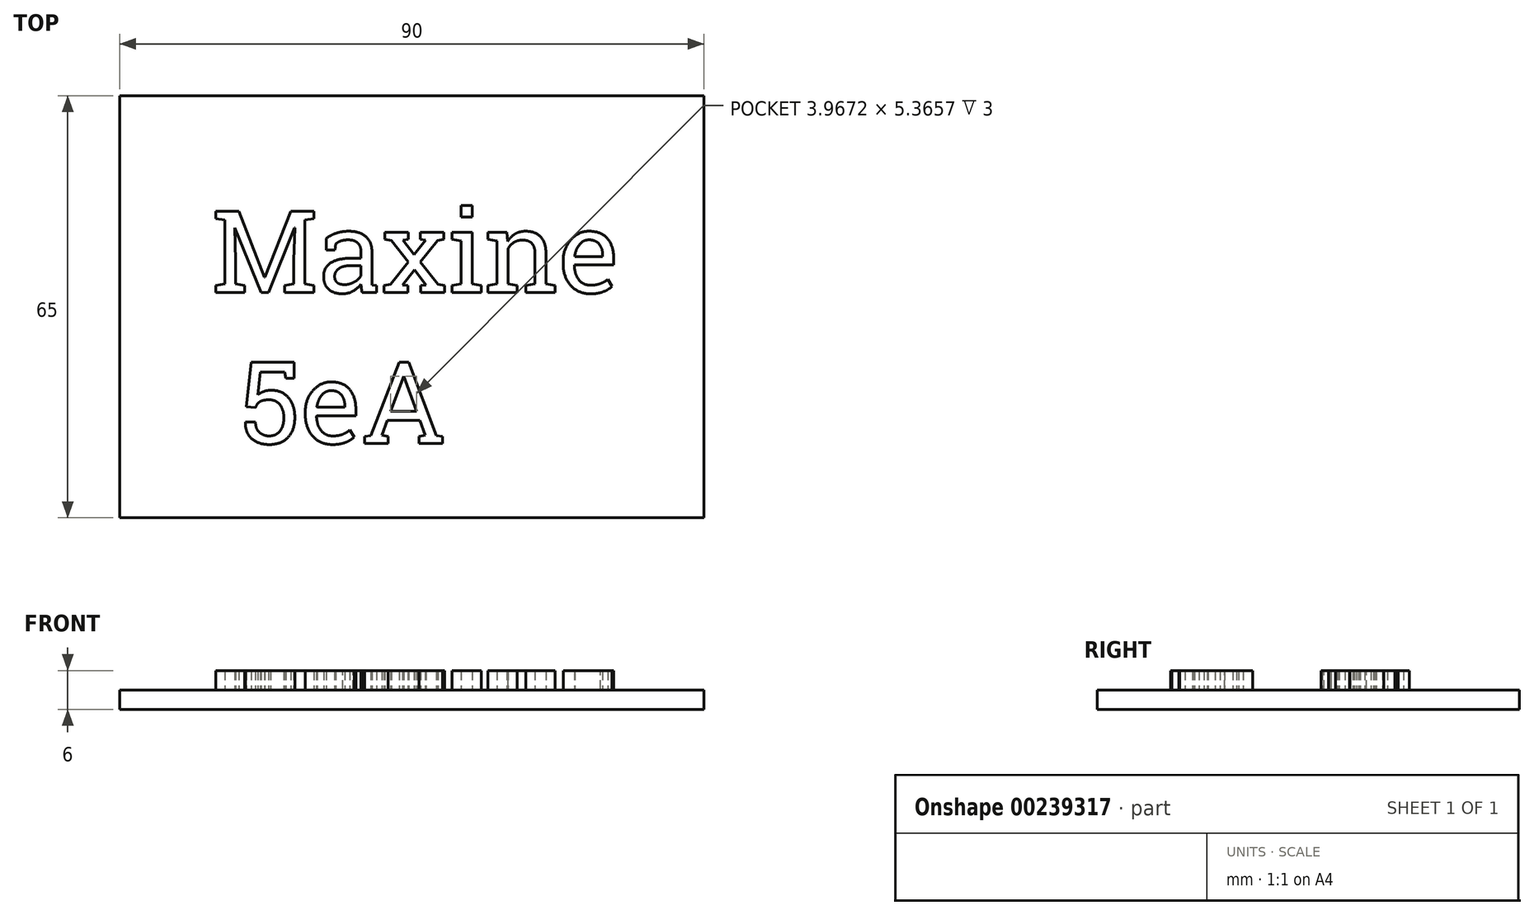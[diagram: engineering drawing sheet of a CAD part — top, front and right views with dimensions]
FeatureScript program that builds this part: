
annotation { "Feature Type Name" : "Feature", "Feature Type Description" : "" }
export const myFeature = defineFeature(function(context is Context, id is Id, definition is map)
    precondition{}
    {
        {
            var Q0;
            Q0=qCreatedBy(makeId("Top.planeOp"),FACE);
            var sketch = newSketch(context, id + "F0", { "sketchPlane" : qUnion([Q0])});
            skLineSegment(sketch, "E0.bottom", {"start": v(0, 0) * mm, "end": v(90, 0) * mm});
            skLineSegment(sketch, "E0.top", {"start": v(0, -65) * mm, "end": v(90, -65) * mm});
            skLineSegment(sketch, "E0.left", {"start": v(0, 0) * mm, "end": v(0, -65) * mm});
            skLineSegment(sketch, "E0.right", {"start": v(90, 0) * mm, "end": v(90, -65) * mm});
            skSolve(sketch);
        }
        {
            var Q0;
            Q0 = qSketchRegion(id + "F0", true);
            extrude(context, id + "F1", {"entities" : qUnion([Q0]), "depth" : 3 * mm});
        }
        {
            var Q0;
            Q0=makeQuery(id+"F1.opExtrude","CAP_FACE",FACE,{"disambiguationData":[OSD([sQuery(id+"F0.wireOp",EDGE,"E0.bottom"),sQuery(id+"F0.wireOp",EDGE,"E0.top"),sQuery(id+"F0.wireOp",EDGE,"E0.left"),sQuery(id+"F0.wireOp",EDGE,"E0.right")])],"isStart":false});
            var sketch = newSketch(context, id + "F2", { "sketchPlane" : qUnion([Q0])});
            skText(sketch, "E1", { "text": "Maxine\n 5eA", "fontName": "RobotoSlab-Regular.ttf"});
            const initialGuessF2  = {"E1": [0.01417, -0.03032, 1, 0, 0.01266]};
            skSetInitialGuess(sketch, initialGuessF2);
            skSolve(sketch);
        }
        {
            var Q0;
            Q0 = qSketchRegion(id + "F2", true);
            extrude(context, id + "F3", {"entities" : qUnion([Q0]), "operationType" : NewBodyOperationType.ADD, "depth" : 3 * mm});
        }
    });
